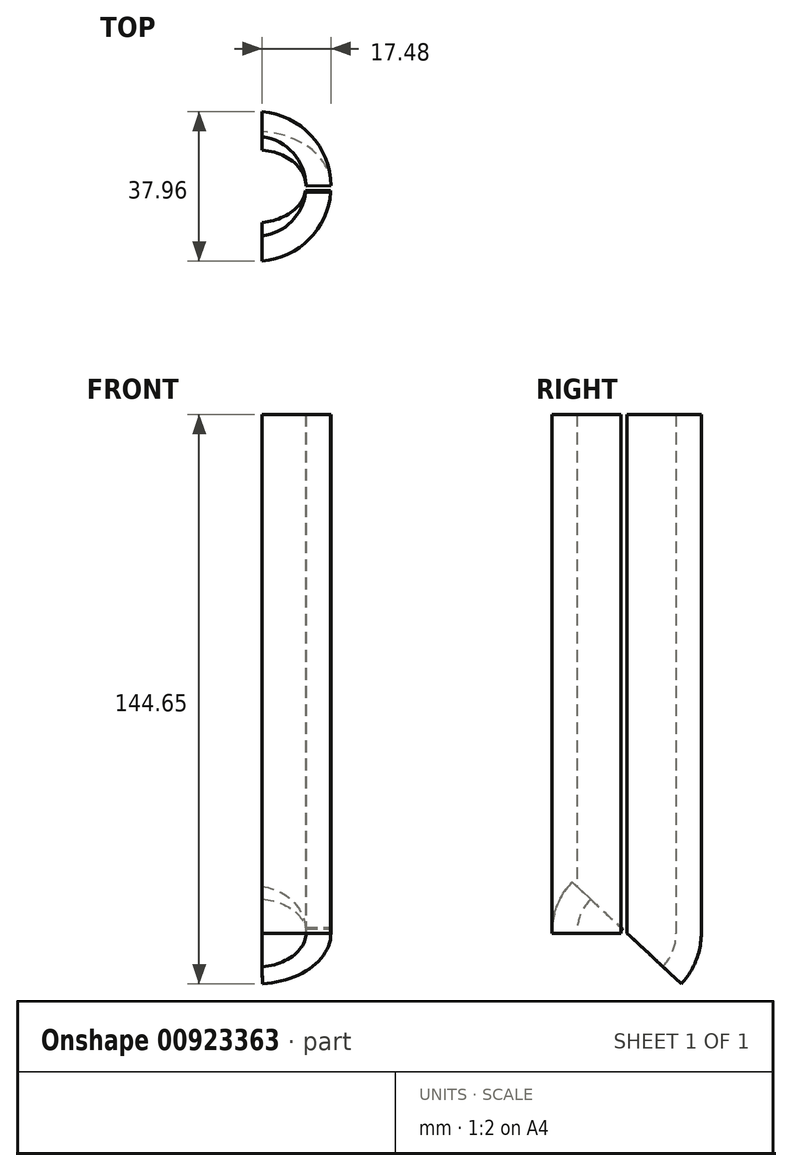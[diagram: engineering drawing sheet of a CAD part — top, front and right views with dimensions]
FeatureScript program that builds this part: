
annotation { "Feature Type Name" : "Feature", "Feature Type Description" : "" }
export const myFeature = defineFeature(function(context is Context, id is Id, definition is map)
    precondition{}
    {
        {
            var Q0;
            Q0=qCreatedBy(makeId("Top.planeOp"),FACE);
            var sketch = newSketch(context, id + "F0", { "sketchPlane" : qUnion([Q0])});
            skCircle(sketch, "E0", {"center": v(0, 0) * mm, "radius": 19.05 * mm});
            skCircle(sketch, "E1", {"center": v(0, 0) * mm, "radius": 12.7 * mm});
            skLineSegment(sketch, "E2", {"start": v(0, 26) * mm, "end": v(0, -46.34) * mm});
            skLineSegment(sketch, "E3", {"start": v(-25.03, 0) * mm, "end": v(32.81, 0.18) * mm});
            skLineSegment(sketch, "E4.0", {"start": v(-25.03, -1.59) * mm, "end": v(32.82, -1.4) * mm});
            skLineSegment(sketch, "E5.0", {"start": v(-25.04, 1.59) * mm, "end": v(32.8, 1.77) * mm});
            skLineSegment(sketch, "E6.0", {"start": v(-1.59, 26) * mm, "end": v(-1.59, -46.34) * mm});
            skLineSegment(sketch, "E7.0", {"start": v(1.59, 26) * mm, "end": v(1.59, -46.34) * mm});
            skSolve(sketch);
        }
        {
            var Q0;
            {var subQ0=sQuery(id+"F0.wireOp",EDGE,"E5.0");var subQ1=sQuery(id+"F0.wireOp",EDGE,"E0");var subQ2=makeQuery(id+"F0.imprint","INTERSECT",VERTEX,{"disambiguationData":[OD(0.0)],"derivedFrom":[subQ1,subQ0]});Q0=makeQuery(id+"F0.imprint","IMPRINT",FACE,{"disambiguationData":[TD([[makeQuery(id+"F0.imprint","IMPRINT",EDGE,{"disambiguationData":[TD([[subQ2,-1.0]])],"derivedFrom":subQ1}),1.0]])]});}
            extrude(context, id + "F1", {"entities" : qUnion([Q0]), "depth" : 149.22 * mm - 19.05 * mm, "offsetDistance" : 30.48 * mm});
        }
        {
            var Q0;
            Q0=makeQuery(id+"F1.opExtrude","CAP_FACE",FACE,{"disambiguationData":[OSD([sQuery(id+"F0.wireOp",EDGE,"E0"),sQuery(id+"F0.wireOp",EDGE,"E1"),sQuery(id+"F0.wireOp",EDGE,"E5.0"),sQuery(id+"F0.wireOp",EDGE,"E7.0")])],"isStart":false});
            extrude(context, id + "F2", {"entities" : qUnion([Q0]), "depth" : 1.59 * mm, "offsetDistance" : 30.48 * mm});
        }
        {
            var Q0;
            {var subQ0=sQuery(id+"F0.wireOp",EDGE,"E7.0");var subQ1=sQuery(id+"F0.wireOp",EDGE,"E0");var subQ2=makeQuery(id+"F0.imprint","INTERSECT",VERTEX,{"disambiguationData":[OD(0.0)],"derivedFrom":[subQ1,subQ0]});Q0=makeQuery(id+"F0.imprint","IMPRINT",FACE,{"disambiguationData":[TD([[makeQuery(id+"F0.imprint","IMPRINT",EDGE,{"disambiguationData":[TD([[subQ2,-1.0]])],"derivedFrom":subQ1}),1.0]])]});}
            var Q1;
            {var subQ0=sQuery(id+"F0.wireOp",EDGE,"E5.0");var subQ1=sQuery(id+"F0.wireOp",EDGE,"E0");var subQ2=makeQuery(id+"F0.imprint","INTERSECT",VERTEX,{"disambiguationData":[OD(0.0)],"derivedFrom":[subQ1,subQ0]});Q1=makeQuery(id+"F0.imprint","IMPRINT",FACE,{"disambiguationData":[TD([[makeQuery(id+"F0.imprint","IMPRINT",EDGE,{"disambiguationData":[TD([[subQ2,1.0]])],"derivedFrom":subQ1}),1.0]])]});}
            extrude(context, id + "F3", {"entities" : qUnion([Q0, Q1]), "operationType" : NewBodyOperationType.ADD, "depth" : 150.8 * mm - 19.05 * mm, "offsetDistance" : 30.48 * mm});
        }
        {
            var Q0;
            Q0=makeQuery(id+"F3.opExtrude","CAP_FACE",FACE,{"disambiguationData":[OSD([sQuery(id+"F0.wireOp",EDGE,"E0"),sQuery(id+"F0.wireOp",EDGE,"E1"),sQuery(id+"F0.wireOp",EDGE,"E3"),sQuery(id+"F0.wireOp",EDGE,"E5.0")])],"isStart":true});
            var Q1;
            Q1=makeQuery(id+"F1.opExtrude","CAP_FACE",FACE,{"disambiguationData":[OSD([sQuery(id+"F0.wireOp",EDGE,"E0"),sQuery(id+"F0.wireOp",EDGE,"E1"),sQuery(id+"F0.wireOp",EDGE,"E5.0"),sQuery(id+"F0.wireOp",EDGE,"E7.0")])],"isStart":true});
            var Q2;
            Q2=makeQuery(id+"F3.opExtrude","CAP_FACE",FACE,{"disambiguationData":[OSD([sQuery(id+"F0.wireOp",EDGE,"E0"),sQuery(id+"F0.wireOp",EDGE,"E1"),sQuery(id+"F0.wireOp",EDGE,"E2"),sQuery(id+"F0.wireOp",EDGE,"E7.0")])],"isStart":true});
            var Q3;
            Q3=makeQuery(id+"F3.opExtrude","CAP_EDGE",EDGE,{"disambiguationData":[OSD([sQuery(id+"F0.wireOp",EDGE,"E3")])],"isStart":true});
            revolve(context, id + "F4", {"operationType" : NewBodyOperationType.ADD, "surfaceOperationType" : NewSurfaceOperationType.NEW, "entities" : qUnion([Q0, Q1, Q2]), "axis" : qUnion([Q3]), "revolveType" : RevolveType.ONE_DIRECTION, "oppositeDirection" : true, "angle" : 43 * degree});
        }
    });
